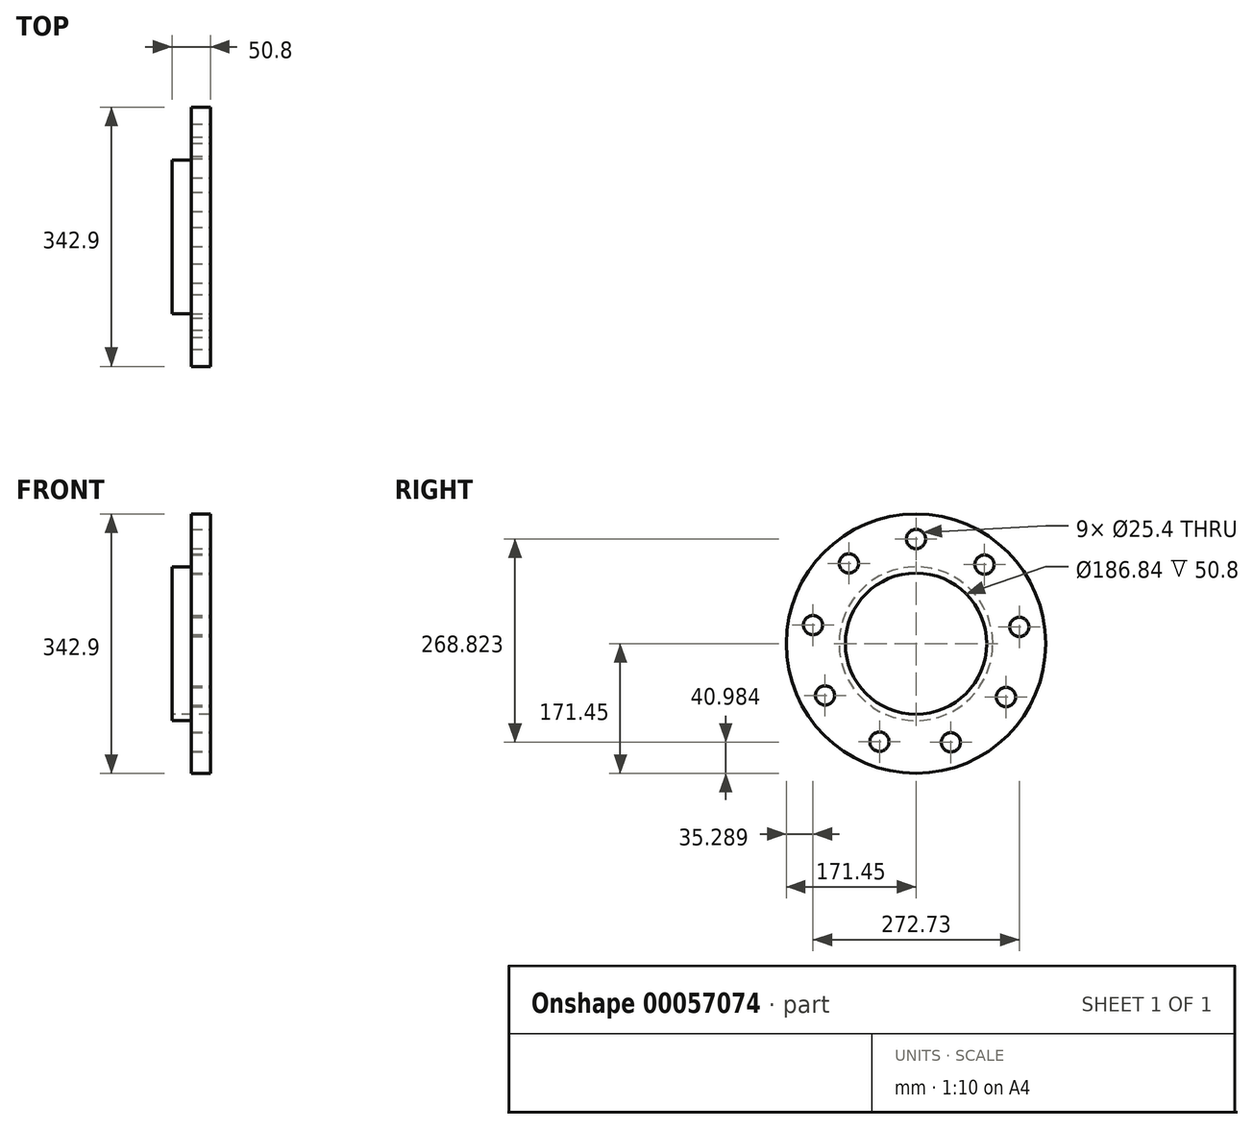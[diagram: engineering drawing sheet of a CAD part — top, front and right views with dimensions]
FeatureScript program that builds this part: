
annotation { "Feature Type Name" : "Feature", "Feature Type Description" : "" }
export const myFeature = defineFeature(function(context is Context, id is Id, definition is map)
    precondition{}
    {
        {
            var Q0;
            Q0=qCreatedBy(makeId("Top.planeOp"),FACE);
            var sketch = newSketch(context, id + "F0", { "sketchPlane" : qUnion([Q0])});
            skCircle(sketch, "E0", {"center": v(0, 0) * mm, "radius": 101.6 * mm});
            skCircle(sketch, "E1", {"center": v(0, 0) * mm, "radius": 93.42 * mm});
            skSolve(sketch);
        }
        {
            var Q0;
            Q0=qCreatedBy(makeId("Front.planeOp"),FACE);
            var sketch = newSketch(context, id + "F1", { "sketchPlane" : qUnion([Q0])});
            skArc(sketch, "E2", {"start": v(0, 0) * mm, "mid": v(89.27, 215.53) * mm, "end": v(304.8, 304.8) * mm});
            skSolve(sketch);
        }
        {
            var Q0;
            Q0=makeQuery(id+"F0.imprint","IMPRINT",FACE,{"disambiguationData":[TD([[makeQuery(id+"F0.imprint","IMPRINT",EDGE,{"derivedFrom":sQuery(id+"F0.wireOp",EDGE,"E0")}),1.0]])]});
            var Q1;
            Q1=sQuery(id+"F1.wireOp",EDGE,"E2");
            sweep(context, id + "F2", {"profiles" : qUnion([Q0]), "path" : qUnion([Q1])});
        }
        {
            var Q0;
            Q0=makeQuery(id+"F2.opSweep","CAP_FACE",FACE,{"disambiguationData":[OSD([sQuery(id+"F0.wireOp",EDGE,"E0"),sQuery(id+"F0.wireOp",EDGE,"E1"),sQuery(id+"F1.wireOp",VERTEX,"E2.end")])],"isStart":false});
            extrude(context, id + "F3", {"entities" : qUnion([Q0]), "operationType" : NewBodyOperationType.ADD, "depth" : 25.4 * mm});
        }
        {
            var Q0;
            Q0=makeQuery(id+"F3.opExtrude","CAP_FACE",FACE,{"disambiguationData":[OSD([sQuery(id+"F0.wireOp",EDGE,"E0"),sQuery(id+"F0.wireOp",EDGE,"E1"),sQuery(id+"F1.wireOp",VERTEX,"E2.end")])],"isStart":false});
            var sketch = newSketch(context, id + "F4", { "sketchPlane" : qUnion([Q0])});
            skCircle(sketch, "E3", {"center": v(0, 304.8) * mm, "radius": 171.45 * mm});
            skCircle(sketch, "E4", {"center": v(0, 304.8) * mm, "radius": 93.42 * mm});
            skSolve(sketch);
        }
        {
            var Q0;
            Q0=qSketchRegion(id+"F4",true);
            extrude(context, id + "F5", {"entities" : qUnion([Q0]), "depth" : 25.4 * mm});
        }
        {
            var Q0;
            Q0=makeQuery(id+"F2.opSweep","CAP_EDGE",EDGE,{"disambiguationData":[OSD([sQuery(id+"F0.wireOp",EDGE,"E0"),sQuery(id+"F1.wireOp",VERTEX,"E2.start")])],"isStart":true});
            chamfer(context, id + "F6", {"entities" : qUnion([Q0]), "width" : 5.08 * mm, "tangentPropagation" : true});
        }
        {
            var Q0;
            Q0=makeQuery(id+"F5.opExtrude","CAP_FACE",FACE,{"disambiguationData":[OSD([sQuery(id+"F4.wireOp",EDGE,"E3"),sQuery(id+"F4.wireOp",EDGE,"E4")])],"isStart":false});
            var sketch = newSketch(context, id + "F7", { "sketchPlane" : qUnion([Q0])});
            skArc(sketch, "E5", {"start": v(2.41, 443.14) * mm, "mid": v(1.2, 443.15) * mm, "end": v(0, 443.16) * mm});
            skPoint(sketch, "E6.orphan", {"position": v(0, 443.16) * mm});
            skPoint(sketch, "E7.start.orphan", {"position": v(138.36, 304.8) * mm});
            skCircle(sketch, "E8", {"center": v(0, 443.16) * mm, "radius": 12.7 * mm});
            skLineSegment(sketch, "E9.anchor1", {"start": v(0, 304.8) * mm, "end": v(0, 443.16) * mm, "construction": true});
            skLineSegment(sketch, "E9.anchor2", {"start": v(0, 304.8) * mm, "end": v(0, 443.16) * mm, "construction": true});
            skCircle(sketch, "E10.1.0", {"center": v(-88.73, 410.96) * mm, "radius": 12.7 * mm});
            skCircle(sketch, "E10.2.0", {"center": v(-136.16, 329.35) * mm, "radius": 12.7 * mm});
            skCircle(sketch, "E10.3.0", {"center": v(-120.22, 236.32) * mm, "radius": 12.7 * mm});
            skCircle(sketch, "E10.4.0", {"center": v(-48.33, 175.16) * mm, "radius": 12.7 * mm});
            skCircle(sketch, "E10.5.0", {"center": v(46.06, 174.33) * mm, "radius": 12.7 * mm});
            skCircle(sketch, "E10.6.0", {"center": v(119, 234.23) * mm, "radius": 12.7 * mm});
            skCircle(sketch, "E10.7.0", {"center": v(136.57, 326.97) * mm, "radius": 12.7 * mm});
            skCircle(sketch, "E10.8.0", {"center": v(90.57, 409.4) * mm, "radius": 12.7 * mm});
            skLineSegment(sketch, "E10.anchor2", {"start": v(0, 304.8) * mm, "end": v(2.41, 443.14) * mm, "construction": true});
            skSolve(sketch);
        }
        {
            var Q0;
            Q0=makeQuery(id+"F7.imprint","IMPRINT",FACE,{"disambiguationData":[TD([[makeQuery(id+"F7.imprint","IMPRINT",EDGE,{"derivedFrom":sQuery(id+"F7.wireOp",EDGE,"E10.1.0")}),1.0]])]});
            var Q1;
            Q1=makeQuery(id+"F7.imprint","IMPRINT",FACE,{"disambiguationData":[TD([[makeQuery(id+"F7.imprint","IMPRINT",EDGE,{"derivedFrom":sQuery(id+"F7.wireOp",EDGE,"E8")}),1.0]])]});
            var Q2;
            Q2=makeQuery(id+"F7.imprint","IMPRINT",FACE,{"disambiguationData":[TD([[makeQuery(id+"F7.imprint","IMPRINT",EDGE,{"derivedFrom":sQuery(id+"F7.wireOp",EDGE,"E10.8.0")}),1.0]])]});
            var Q3;
            Q3=makeQuery(id+"F7.imprint","IMPRINT",FACE,{"disambiguationData":[TD([[makeQuery(id+"F7.imprint","IMPRINT",EDGE,{"derivedFrom":sQuery(id+"F7.wireOp",EDGE,"E10.7.0")}),1.0]])]});
            var Q4;
            Q4=makeQuery(id+"F7.imprint","IMPRINT",FACE,{"disambiguationData":[TD([[makeQuery(id+"F7.imprint","IMPRINT",EDGE,{"derivedFrom":sQuery(id+"F7.wireOp",EDGE,"E10.6.0")}),1.0]])]});
            var Q5;
            Q5=makeQuery(id+"F7.imprint","IMPRINT",FACE,{"disambiguationData":[TD([[makeQuery(id+"F7.imprint","IMPRINT",EDGE,{"derivedFrom":sQuery(id+"F7.wireOp",EDGE,"E10.5.0")}),1.0]])]});
            var Q6;
            Q6=makeQuery(id+"F7.imprint","IMPRINT",FACE,{"disambiguationData":[TD([[makeQuery(id+"F7.imprint","IMPRINT",EDGE,{"derivedFrom":sQuery(id+"F7.wireOp",EDGE,"E10.4.0")}),1.0]])]});
            var Q7;
            Q7=makeQuery(id+"F7.imprint","IMPRINT",FACE,{"disambiguationData":[TD([[makeQuery(id+"F7.imprint","IMPRINT",EDGE,{"derivedFrom":sQuery(id+"F7.wireOp",EDGE,"E10.3.0")}),1.0]])]});
            var Q8;
            Q8=makeQuery(id+"F7.imprint","IMPRINT",FACE,{"disambiguationData":[TD([[makeQuery(id+"F7.imprint","IMPRINT",EDGE,{"derivedFrom":sQuery(id+"F7.wireOp",EDGE,"E10.2.0")}),1.0]])]});
            extrude(context, id + "F8", {"entities" : qUnion([Q0, Q1, Q2, Q3, Q4, Q5, Q6, Q7, Q8]), "operationType" : NewBodyOperationType.REMOVE, "endBound" : BoundingType.THROUGH_ALL, "oppositeDirection" : true, "depth" : 25.4 * mm});
        }
        {
            var Q0;
            Q0=makeQuery(id+"F2.opSweep","SWEPT_BODY",BODY,{"disambiguationData":[OSD([sQuery(id+"F0.wireOp",EDGE,"E0"),sQuery(id+"F0.wireOp",EDGE,"E1"),sQuery(id+"F1.wireOp",EDGE,"E2")])]});
            deleteBodies(context, id + "F9", {"entities" : qUnion([Q0])});
        }
        {
            var Q0;
            Q0=makeQuery(id+"F5.opExtrude","CAP_FACE",FACE,{"disambiguationData":[OSD([sQuery(id+"F4.wireOp",EDGE,"E3"),sQuery(id+"F4.wireOp",EDGE,"E4")])],"isStart":true});
            var sketch = newSketch(context, id + "F10", { "sketchPlane" : qUnion([Q0])});
            skCircle(sketch, "E11", {"center": v(0, 304.8) * mm, "radius": 101.6 * mm});
            skCircle(sketch, "E12", {"center": v(0, 304.8) * mm, "radius": 93.42 * mm});
            skSolve(sketch);
        }
        {
            var Q0;
            Q0=makeQuery(id+"F10.imprint","IMPRINT",FACE,{"disambiguationData":[TD([[makeQuery(id+"F10.imprint","IMPRINT",EDGE,{"derivedFrom":sQuery(id+"F10.wireOp",EDGE,"E11")}),1.0]])]});
            extrude(context, id + "F11", {"entities" : qUnion([Q0]), "operationType" : NewBodyOperationType.ADD, "depth" : 25.4 * mm});
        }
    });
